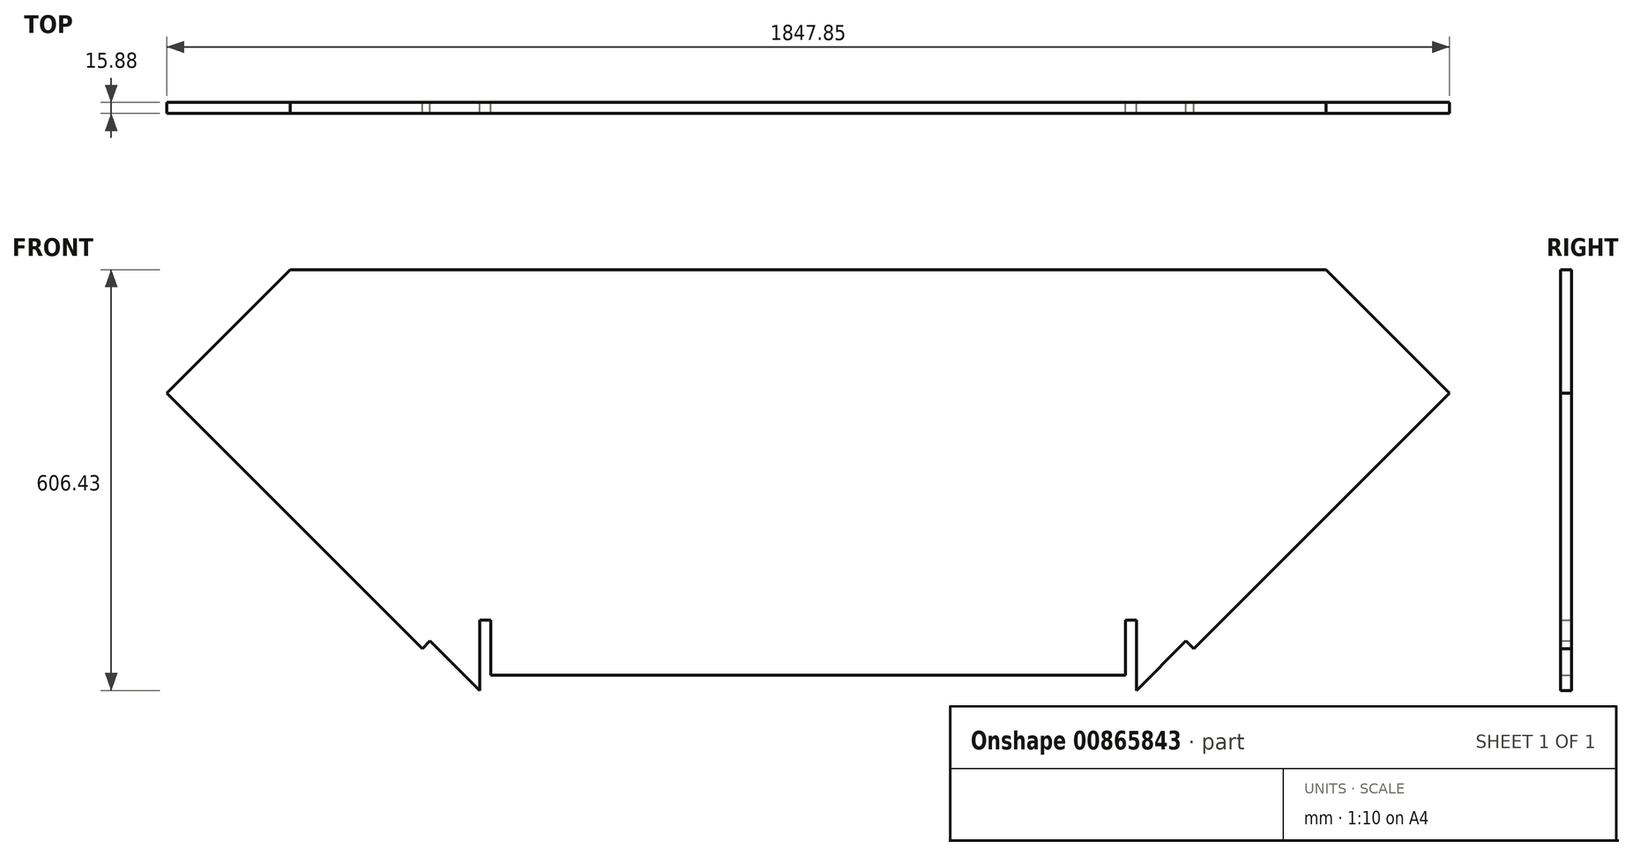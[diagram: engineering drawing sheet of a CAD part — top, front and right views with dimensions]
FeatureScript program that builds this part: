
annotation { "Feature Type Name" : "Feature", "Feature Type Description" : "" }
export const myFeature = defineFeature(function(context is Context, id is Id, definition is map)
    precondition{}
    {
        {
            var Q0;
            Q0=qCreatedBy(makeId("Front.planeOp"),FACE);
            var sketch = newSketch(context, id + "F0", { "sketchPlane" : qUnion([Q0])});
            skLineSegment(sketch, "E0", {"start": v(-67.21, -20.95) * mm, "end": v(847.19, -20.95) * mm});
            skLineSegment(sketch, "E1", {"start": v(847.19, -20.95) * mm, "end": v(847.19, 58.42) * mm});
            skLineSegment(sketch, "E2", {"start": v(-67.21, 58.42) * mm, "end": v(-67.21, -20.95) * mm});
            skLineSegment(sketch, "E3", {"start": v(847.19, 58.42) * mm, "end": v(863.06, 58.42) * mm});
            skLineSegment(sketch, "E4", {"start": v(863.06, 58.42) * mm, "end": v(863.06, -43.18) * mm});
            skLineSegment(sketch, "E5", {"start": v(-67.21, -20.95) * mm, "end": v(-67.21, 58.42) * mm});
            skLineSegment(sketch, "E6", {"start": v(-67.21, 58.42) * mm, "end": v(-83.09, 58.42) * mm});
            skLineSegment(sketch, "E7", {"start": v(-83.09, 58.42) * mm, "end": v(-83.09, -43.18) * mm});
            skLineSegment(sketch, "E8", {"start": v(-356.14, 563.25) * mm, "end": v(-533.94, 385.45) * mm});
            skLineSegment(sketch, "E9", {"start": v(1136.11, 563.25) * mm, "end": v(1313.91, 385.45) * mm});
            skLineSegment(sketch, "E10", {"start": v(1313.91, 385.45) * mm, "end": v(945.72, 17.26) * mm});
            skLineSegment(sketch, "E11", {"start": v(-533.94, 385.45) * mm, "end": v(-165.75, 17.26) * mm});
            skLineSegment(sketch, "E12", {"start": v(-165.75, 17.26) * mm, "end": v(-154.52, 28.48) * mm});
            skLineSegment(sketch, "E13", {"start": v(-154.52, 28.48) * mm, "end": v(-83.09, -43.18) * mm});
            skLineSegment(sketch, "E14", {"start": v(945.72, 17.26) * mm, "end": v(934.5, 28.48) * mm});
            skLineSegment(sketch, "E15", {"start": v(934.5, 28.48) * mm, "end": v(863.06, -43.18) * mm});
            skLineSegment(sketch, "E16", {"start": v(-356.14, 563.25) * mm, "end": v(1136.11, 563.25) * mm});
            skSolve(sketch);
        }
        {
            var Q0;
            Q0 = qSketchRegion(id + "F0", true);
            extrude(context, id + "F1", {"entities" : qUnion([Q0]), "depth" : 15.88 * mm, "offsetDistance" : 25.4 * mm});
        }
    });
